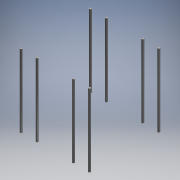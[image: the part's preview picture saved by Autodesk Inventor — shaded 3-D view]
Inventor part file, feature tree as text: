
AUTODESK INVENTOR PART (.ipt)
format: ipt  version: 2018 (Build 220112000, 112)  size: 115,712 bytes
history: native  units: in
note: dims shown in document units (in); Inventor stores cm internally (conversion verified against a paired STEP export)
features: extrude x1, sketch x1
ambient origin geometry x8: Origin, YZ Plane, XZ Plane, XY Plane, X Axis, Y Axis, Z Axis, Center Point
bodies: Solid1 (feature_tree)
feature tree (2):
  extrude  "Extrusion1"  Depth=84.0in
  sketch  "Sketch1"  dims[d0=2.5in d1=72.0in d2=84.0in d3=2.0in d4=2.5in d5=2.5in d6=21.0in d7=2.0in d8=0.7874in d10=80.0in d11=0.7874in d13=79.0in d16=0.7874in d18=80.0in d19=0.7874in d21=42.0in d24=84.0in d25=0.0in]
